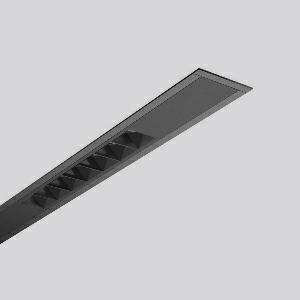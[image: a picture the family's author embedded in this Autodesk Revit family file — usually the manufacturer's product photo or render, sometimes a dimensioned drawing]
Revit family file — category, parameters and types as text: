
# Revit family: less_is_more_beamline_312474_003_fc7e
name_source: partatom
category: Lighting Fixtures
units: mm (PartAtom-declared; Revit-internal decimal feet)

## family parameters
Cut with Voids When Loaded = No
Host = Face
Light Source = No
Part Type = Normal
Room Calculation Point = No
Round Connector Dimension = Use Diameter
Shared = No

## types (1)
- LESS IS MORE BEAMLINE (1 x LED Modul 930, 1783.33 lm, 3000)
    Apparent Load = 72 VA
    CIE Flux Codes = 100 100 100 100 100
    Color Rendering = 90
    Color Temperature = 3000
    Default Elevation = 1800 mm
    Description = Series: LESS IS MORE BEAMLINE
Linear recessed ceiling and wall luminaire for aesthetically sophisticated lighting. Luminaire with three LED light units. Housing: extruded aluminium profile, powder-coated. End cap aluminium powder-coated. LED light unit with MRS technology: Mini-Reflector-System made of metallised thermoplastic with prismatic black glare-suppressing frame for pleasant glare-free light (RUG < 10). Each LED light unit has 7 reflector elements. Narrow beam light distribution. Ceiling installation with pre-assembled SBS mounting system. LED unit with integrated converter interchangeable and removable. Suitable for through-wiring. 
Colour: deep black, matt (RAL 9005)
Length: 1702 mm
Width: 71 mm
Height: 1.5 mm
Cut-out length: 1688 mm
Cut-out width: 60 mm
Recess height: 125 mm
Luminaire: recess height: 106 mm
Lamp: LED
Socket: without socket
Colour temperature: 3000K
Colour rendering index (CRI): 90
System power: 72 W
Rated luminous flux: 5350 lm
Luminous efficiency: 74 lm/W
Control gear: Regulated power supply
Protection class: I
Type of protection: IP 20
    Height = 0 mm  [stored 0 ft]
    Lamp = 1 x LED Modul 930
    Lamp Light Flux = 1783.33 lm
    Lamp count = 1
    Length = 1702 mm
    Lifetime = 50000 h
    Luminous efficacy = 74 lm/W
    Manufacturer = RZB
    ModVariant = No
    Model = 312474.003
    Mounting Place = Ceiling, Wall
    Mounting Type = Recessed
    Number of Poles = 1
    OnlyDefault = Yes
    Power Factor = 1
    Product Name = LESS IS MORE BEAMLINE
    Product group = Recessed LED linear luminaires
    ProductGroupID = 407
    Protection Class = Protection class I
    Protection Degree = IP 20
    RLX_Detail_Level = 1
    RLX_Emergency_Light_Flux = 0 lm
    RLX_Emergency_Type = 0
    RLX_Emergency_Type_DB = No
    RlxData = <blob elided: 24261 chars, md5=115cec79>
    Socket = socket
    Standby Power = 0 W
    System Light Flux = 5350 lm
    System Power = 72 W
    Type Comments = Product without accessories
    Type Image = 312465.003.jpg
    URL = http://relux.com
    VarID = ---
    Voltage = 230 V
    Voltage Range = 220-240 V
    Weight = 0.00 kg
    Width = 71 mm

note: [stored X ft] marks values corroborated as IEEE doubles in the binary element streams (Revit-internal decimal feet)

## geometry (parser evidence)
native form markers: Blend x4, Sweep x18
no freeform markers — native parametric forms only
